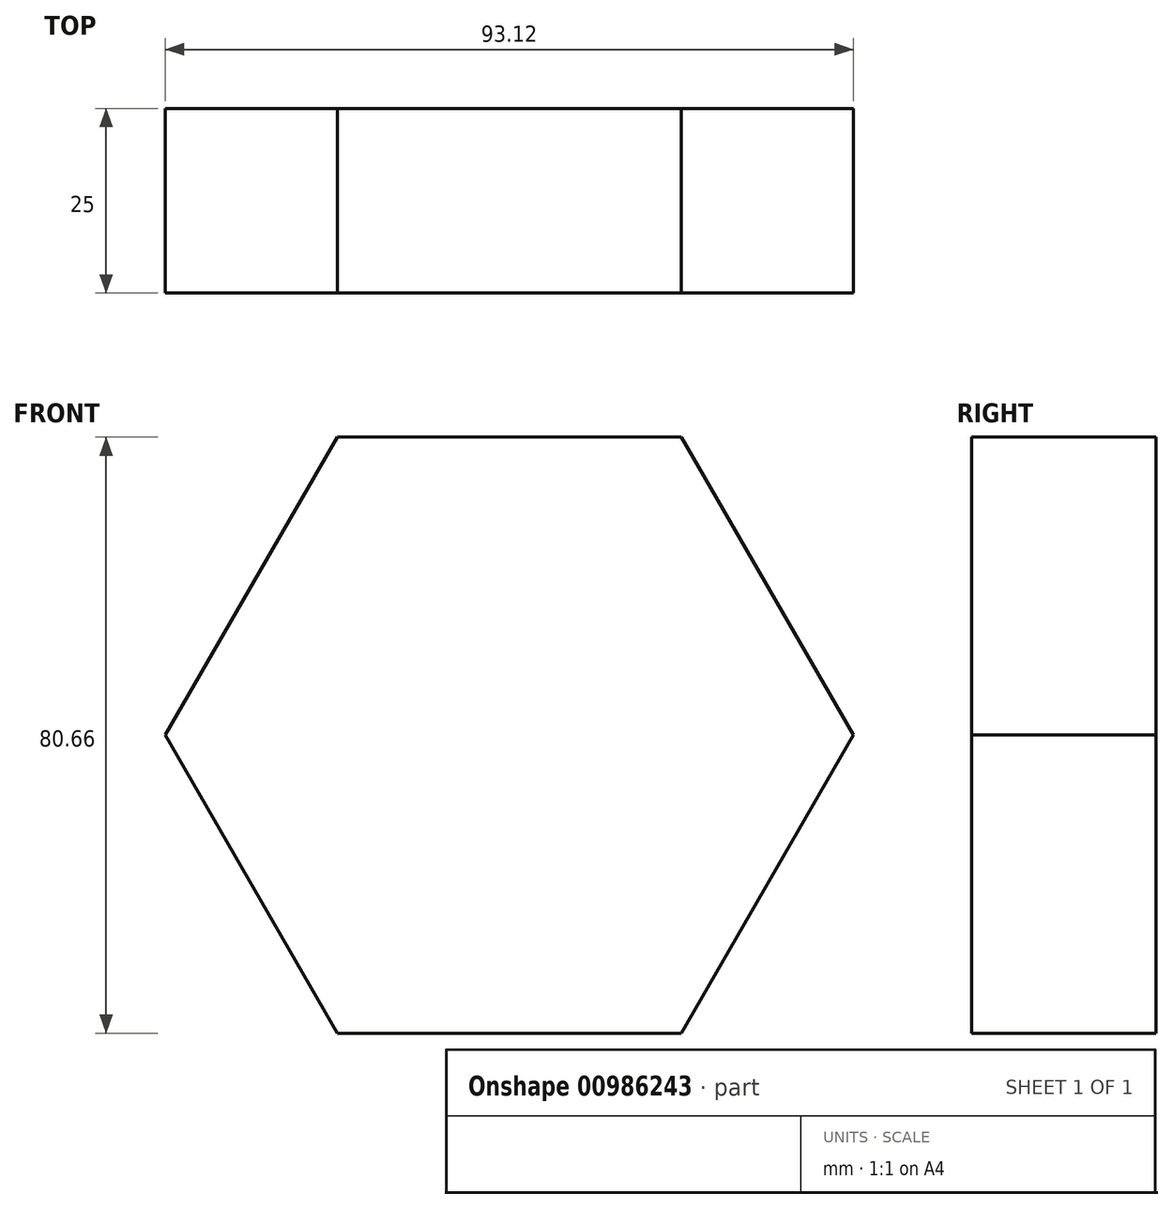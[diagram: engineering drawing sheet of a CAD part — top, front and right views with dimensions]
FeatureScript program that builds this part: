
annotation { "Feature Type Name" : "Feature", "Feature Type Description" : "" }
export const myFeature = defineFeature(function(context is Context, id is Id, definition is map)
    precondition{}
    {
        {
            var Q0;
            Q0=qCreatedBy(makeId("Front.planeOp"),FACE);
            var sketch = newSketch(context, id + "F0", { "sketchPlane" : qUnion([Q0])});
            skCircle(sketch, "E0.cCircle", {"center": v(0, 0) * mm, "radius": 40.33 * mm, "construction": true});
            skLineSegment(sketch, "E0.0", {"start": v(23.28, -40.33) * mm, "end": v(-23.28, -40.33) * mm});
            skLineSegment(sketch, "E0.1", {"start": v(-23.28, -40.33) * mm, "end": v(-46.56, 0) * mm});
            skLineSegment(sketch, "E0.2", {"start": v(-46.56, 0) * mm, "end": v(-23.28, 40.33) * mm});
            skLineSegment(sketch, "E0.3", {"start": v(-23.28, 40.33) * mm, "end": v(23.28, 40.33) * mm});
            skLineSegment(sketch, "E0.4", {"start": v(23.28, 40.33) * mm, "end": v(46.56, 0) * mm});
            skLineSegment(sketch, "E0.5", {"start": v(46.56, 0) * mm, "end": v(23.28, -40.33) * mm});
            skPoint(sketch, "E0.0.midPoint", {"position": v(0, -40.33) * mm});
            skSolve(sketch);
        }
        {
            var Q0;
            Q0=makeQuery(id+"F0.imprint","IMPRINT",FACE,{"disambiguationData":[TD([[makeQuery(id+"F0.imprint","IMPRINT",EDGE,{"derivedFrom":sQuery(id+"F0.wireOp",EDGE,"E0.0")}),-1.0]])]});
            extrude(context, id + "F1", {"entities" : qUnion([Q0]), "depth" : 25 * mm, "offsetDistance" : 25 * mm});
        }
    });
